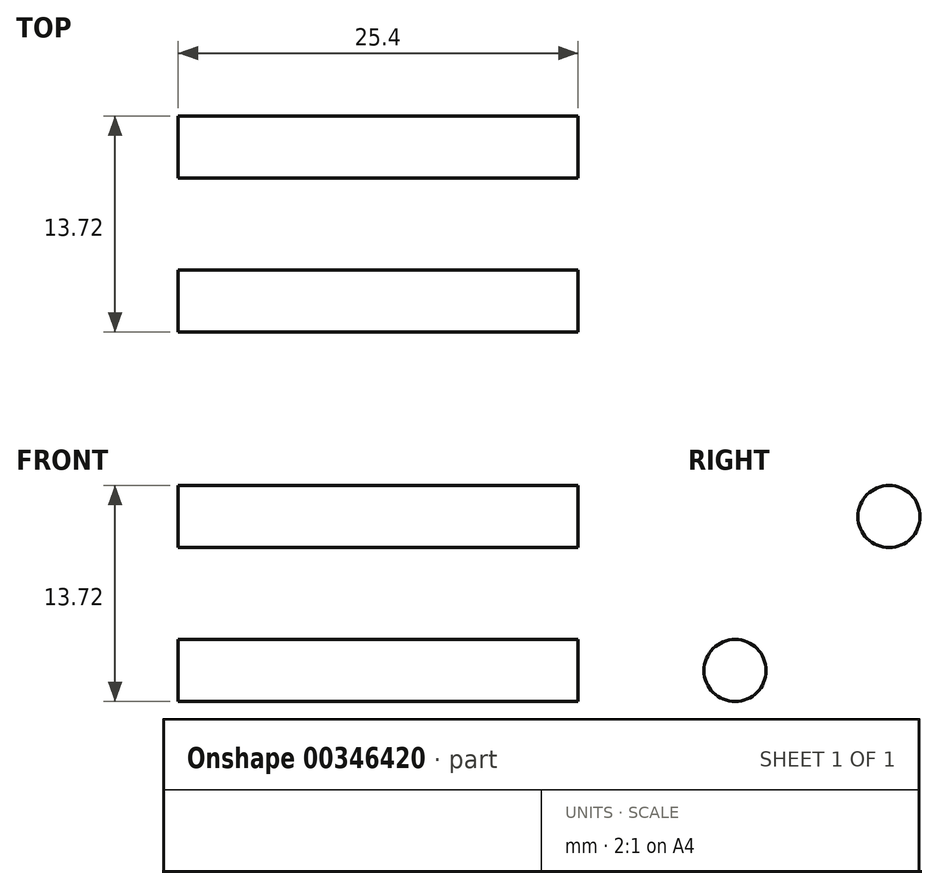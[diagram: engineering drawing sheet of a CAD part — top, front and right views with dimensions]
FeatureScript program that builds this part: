
annotation { "Feature Type Name" : "Feature", "Feature Type Description" : "" }
export const myFeature = defineFeature(function(context is Context, id is Id, definition is map)
    precondition{}
    {
        {
            var Q0;
            Q0=qCreatedBy(makeId("Front.planeOp"),FACE);
            var sketch = newSketch(context, id + "F0", { "sketchPlane" : qUnion([Q0])});
            skLineSegment(sketch, "E0.top", {"start": v(-34.36, 16.13) * mm, "end": v(-8.96, 16.13) * mm});
            skLineSegment(sketch, "E0.left", {"start": v(-34.36, 32) * mm, "end": v(-34.36, 16.13) * mm});
            skLineSegment(sketch, "E0.right", {"start": v(-8.96, 32) * mm, "end": v(-8.96, 16.13) * mm});
            skLineSegment(sketch, "E1", {"start": v(-34.36, 32) * mm, "end": v(-31.05, 32) * mm});
            skLineSegment(sketch, "E2", {"start": v(-12.26, 32) * mm, "end": v(-8.96, 32) * mm});
            skEllipticalArc(sketch, "E3", {});
            skPoint(sketch, "E4.visualSharp", {"position": v(-29.28, 32) * mm});
            skArc(sketch, "E4.filletArc", {"start": v(-28.9, 30.84) * mm, "mid": v(-29.83, 31.7) * mm, "end": v(-31.05, 32) * mm});
            skPoint(sketch, "E5.visualSharp", {"position": v(-14.04, 32) * mm});
            skArc(sketch, "E5.filletArc", {"start": v(-12.26, 32) * mm, "mid": v(-13.48, 31.7) * mm, "end": v(-14.4, 30.84) * mm});
            const initialGuessF0  = {"E3": [-0.02165555876195431, 0.03200357941810279, -1, 0, 0.00762, 0.00381, 0.3110816848913883, 2.8305109686984053]};
            skSetInitialGuess(sketch, initialGuessF0);
            skSolve(sketch);
        }
        {
            var Q0;
            Q0=makeQuery(id+"F0.imprint","IMPRINT",FACE,{"disambiguationData":[TD([[makeQuery(id+"F0.imprint","IMPRINT",EDGE,{"derivedFrom":sQuery(id+"F0.wireOp",EDGE,"E0.top")}),1.0]])]});
            var Q1;
            Q1=sQuery(id+"F0.wireOp",EDGE,"E0.top");
            revolve(context, id + "F1", {"entities" : qUnion([Q0]), "axis" : qUnion([Q1]), "revolveType" : RevolveType.FULL});
        }
        {
            var Q0;
            Q0=makeQuery(id+"F1.opRevolve","SWEPT_FACE",FACE,{"disambiguationData":[OSD([sQuery(id+"F0.wireOp",EDGE,"E0.right")])]});
            var sketch = newSketch(context, id + "F2", { "sketchPlane" : qUnion([Q0])});
            skCircle(sketch, "E6", {"center": v(0, 16.13) * mm, "radius": 9.78 * mm});
            skCircle(sketch, "E7", {"center": v(9.78, 16.13) * mm, "radius": 1.97 * mm});
            skCircle(sketch, "E8.1.0", {"center": v(6.91, 23.04) * mm, "radius": 1.97 * mm});
            skCircle(sketch, "E8.2.0", {"center": v(0, 25.9) * mm, "radius": 1.97 * mm});
            skCircle(sketch, "E8.3.0", {"center": v(-6.91, 23.04) * mm, "radius": 1.97 * mm});
            skCircle(sketch, "E8.4.0", {"center": v(-9.78, 16.13) * mm, "radius": 1.97 * mm});
            skCircle(sketch, "E8.5.0", {"center": v(-6.91, 9.21) * mm, "radius": 1.97 * mm});
            skCircle(sketch, "E8.6.0", {"center": v(0, 6.35) * mm, "radius": 1.97 * mm});
            skCircle(sketch, "E8.7.0", {"center": v(6.91, 9.21) * mm, "radius": 1.97 * mm});
            skCircle(sketch, "E9", {"center": v(0, 16.13) * mm, "radius": 3.56 * mm});
            skSolve(sketch);
        }
        {
            var Q0;
            {var subQ0=sQuery(id+"F2.wireOp",EDGE,"E8.1.0");var subQ1=sQuery(id+"F2.wireOp",EDGE,"E6");var subQ2=makeQuery(id+"F2.imprint","INTERSECT",VERTEX,{"disambiguationData":[OD(0.0)],"derivedFrom":[subQ1,subQ0]});Q0=makeQuery(id+"F2.imprint","IMPRINT",FACE,{"disambiguationData":[TD([[makeQuery(id+"F2.imprint","IMPRINT",EDGE,{"disambiguationData":[TD([[subQ2,-1.0]])],"derivedFrom":subQ1}),1.0]])]});}
            var Q1;
            {var subQ0=sQuery(id+"F2.wireOp",EDGE,"E8.1.0");var subQ1=sQuery(id+"F2.wireOp",EDGE,"E6");var subQ2=makeQuery(id+"F2.imprint","INTERSECT",VERTEX,{"disambiguationData":[OD(0.0)],"derivedFrom":[subQ1,subQ0]});Q1=makeQuery(id+"F2.imprint","IMPRINT",FACE,{"disambiguationData":[TD([[makeQuery(id+"F2.imprint","IMPRINT",EDGE,{"disambiguationData":[TD([[subQ2,-1.0]])],"derivedFrom":subQ1}),-1.0]])]});}
            var Q2;
            {var subQ0=sQuery(id+"F2.wireOp",EDGE,"E8.2.0");var subQ1=sQuery(id+"F2.wireOp",EDGE,"E6");var subQ2=makeQuery(id+"F2.imprint","INTERSECT",VERTEX,{"disambiguationData":[OD(0.0)],"derivedFrom":[subQ1,subQ0]});Q2=makeQuery(id+"F2.imprint","IMPRINT",FACE,{"disambiguationData":[TD([[makeQuery(id+"F2.imprint","IMPRINT",EDGE,{"disambiguationData":[TD([[subQ2,-1.0]])],"derivedFrom":subQ1}),1.0]])]});}
            var Q3;
            {var subQ0=sQuery(id+"F2.wireOp",EDGE,"E8.2.0");var subQ1=sQuery(id+"F2.wireOp",EDGE,"E6");var subQ2=makeQuery(id+"F2.imprint","INTERSECT",VERTEX,{"disambiguationData":[OD(0.0)],"derivedFrom":[subQ1,subQ0]});Q3=makeQuery(id+"F2.imprint","IMPRINT",FACE,{"disambiguationData":[TD([[makeQuery(id+"F2.imprint","IMPRINT",EDGE,{"disambiguationData":[TD([[subQ2,-1.0]])],"derivedFrom":subQ1}),-1.0]])]});}
            var Q4;
            {var subQ0=sQuery(id+"F2.wireOp",EDGE,"E8.3.0");var subQ1=sQuery(id+"F2.wireOp",EDGE,"E6");var subQ2=makeQuery(id+"F2.imprint","INTERSECT",VERTEX,{"disambiguationData":[OD(0.0)],"derivedFrom":[subQ1,subQ0]});Q4=makeQuery(id+"F2.imprint","IMPRINT",FACE,{"disambiguationData":[TD([[makeQuery(id+"F2.imprint","IMPRINT",EDGE,{"disambiguationData":[TD([[subQ2,-1.0]])],"derivedFrom":subQ1}),1.0]])]});}
            var Q5;
            {var subQ0=sQuery(id+"F2.wireOp",EDGE,"E8.3.0");var subQ1=sQuery(id+"F2.wireOp",EDGE,"E6");var subQ2=makeQuery(id+"F2.imprint","INTERSECT",VERTEX,{"disambiguationData":[OD(0.0)],"derivedFrom":[subQ1,subQ0]});Q5=makeQuery(id+"F2.imprint","IMPRINT",FACE,{"disambiguationData":[TD([[makeQuery(id+"F2.imprint","IMPRINT",EDGE,{"disambiguationData":[TD([[subQ2,-1.0]])],"derivedFrom":subQ1}),-1.0]])]});}
            var Q6;
            {var subQ0=sQuery(id+"F2.wireOp",EDGE,"E8.4.0");var subQ1=sQuery(id+"F2.wireOp",EDGE,"E6");var subQ2=makeQuery(id+"F2.imprint","INTERSECT",VERTEX,{"disambiguationData":[OD(0.0)],"derivedFrom":[subQ1,subQ0]});Q6=makeQuery(id+"F2.imprint","IMPRINT",FACE,{"disambiguationData":[TD([[makeQuery(id+"F2.imprint","IMPRINT",EDGE,{"disambiguationData":[TD([[subQ2,-1.0]])],"derivedFrom":subQ1}),1.0]])]});}
            var Q7;
            {var subQ0=sQuery(id+"F2.wireOp",EDGE,"E8.4.0");var subQ1=sQuery(id+"F2.wireOp",EDGE,"E6");var subQ2=makeQuery(id+"F2.imprint","INTERSECT",VERTEX,{"disambiguationData":[OD(0.0)],"derivedFrom":[subQ1,subQ0]});Q7=makeQuery(id+"F2.imprint","IMPRINT",FACE,{"disambiguationData":[TD([[makeQuery(id+"F2.imprint","IMPRINT",EDGE,{"disambiguationData":[TD([[subQ2,-1.0]])],"derivedFrom":subQ1}),-1.0]])]});}
            var Q8;
            {var subQ0=sQuery(id+"F2.wireOp",EDGE,"E8.5.0");var subQ1=sQuery(id+"F2.wireOp",EDGE,"E6");var subQ2=makeQuery(id+"F2.imprint","INTERSECT",VERTEX,{"disambiguationData":[OD(0.0)],"derivedFrom":[subQ1,subQ0]});Q8=makeQuery(id+"F2.imprint","IMPRINT",FACE,{"disambiguationData":[TD([[makeQuery(id+"F2.imprint","IMPRINT",EDGE,{"disambiguationData":[TD([[subQ2,-1.0]])],"derivedFrom":subQ1}),1.0]])]});}
            var Q9;
            {var subQ0=sQuery(id+"F2.wireOp",EDGE,"E8.5.0");var subQ1=sQuery(id+"F2.wireOp",EDGE,"E6");var subQ2=makeQuery(id+"F2.imprint","INTERSECT",VERTEX,{"disambiguationData":[OD(0.0)],"derivedFrom":[subQ1,subQ0]});Q9=makeQuery(id+"F2.imprint","IMPRINT",FACE,{"disambiguationData":[TD([[makeQuery(id+"F2.imprint","IMPRINT",EDGE,{"disambiguationData":[TD([[subQ2,-1.0]])],"derivedFrom":subQ1}),-1.0]])]});}
            var Q10;
            {var subQ0=sQuery(id+"F2.wireOp",EDGE,"E8.6.0");var subQ1=sQuery(id+"F2.wireOp",EDGE,"E6");var subQ2=makeQuery(id+"F2.imprint","INTERSECT",VERTEX,{"disambiguationData":[OD(0.0)],"derivedFrom":[subQ1,subQ0]});Q10=makeQuery(id+"F2.imprint","IMPRINT",FACE,{"disambiguationData":[TD([[makeQuery(id+"F2.imprint","IMPRINT",EDGE,{"disambiguationData":[TD([[subQ2,-1.0]])],"derivedFrom":subQ1}),1.0]])]});}
            var Q11;
            {var subQ0=sQuery(id+"F2.wireOp",EDGE,"E8.6.0");var subQ1=sQuery(id+"F2.wireOp",EDGE,"E6");var subQ2=makeQuery(id+"F2.imprint","INTERSECT",VERTEX,{"disambiguationData":[OD(0.0)],"derivedFrom":[subQ1,subQ0]});Q11=makeQuery(id+"F2.imprint","IMPRINT",FACE,{"disambiguationData":[TD([[makeQuery(id+"F2.imprint","IMPRINT",EDGE,{"disambiguationData":[TD([[subQ2,-1.0]])],"derivedFrom":subQ1}),-1.0]])]});}
            var Q12;
            {var subQ0=sQuery(id+"F2.wireOp",EDGE,"E8.7.0");var subQ1=sQuery(id+"F2.wireOp",EDGE,"E6");var subQ2=makeQuery(id+"F2.imprint","INTERSECT",VERTEX,{"disambiguationData":[OD(0.0)],"derivedFrom":[subQ1,subQ0]});Q12=makeQuery(id+"F2.imprint","IMPRINT",FACE,{"disambiguationData":[TD([[makeQuery(id+"F2.imprint","IMPRINT",EDGE,{"disambiguationData":[TD([[subQ2,-1.0]])],"derivedFrom":subQ1}),1.0]])]});}
            var Q13;
            {var subQ0=sQuery(id+"F2.wireOp",EDGE,"E8.7.0");var subQ1=sQuery(id+"F2.wireOp",EDGE,"E6");var subQ2=makeQuery(id+"F2.imprint","INTERSECT",VERTEX,{"disambiguationData":[OD(0.0)],"derivedFrom":[subQ1,subQ0]});Q13=makeQuery(id+"F2.imprint","IMPRINT",FACE,{"disambiguationData":[TD([[makeQuery(id+"F2.imprint","IMPRINT",EDGE,{"disambiguationData":[TD([[subQ2,-1.0]])],"derivedFrom":subQ1}),-1.0]])]});}
            var Q14;
            {var subQ0=sQuery(id+"F2.wireOp",EDGE,"E7");var subQ1=sQuery(id+"F2.wireOp",EDGE,"E6");var subQ2=makeQuery(id+"F2.imprint","INTERSECT",VERTEX,{"disambiguationData":[OD(0.0)],"derivedFrom":[subQ1,subQ0]});Q14=makeQuery(id+"F2.imprint","IMPRINT",FACE,{"disambiguationData":[TD([[makeQuery(id+"F2.imprint","IMPRINT",EDGE,{"disambiguationData":[TD([[subQ2,1.0]])],"derivedFrom":subQ1}),1.0]])]});}
            var Q15;
            {var subQ0=sQuery(id+"F2.wireOp",EDGE,"E7");var subQ1=sQuery(id+"F2.wireOp",EDGE,"E6");var subQ2=makeQuery(id+"F2.imprint","INTERSECT",VERTEX,{"disambiguationData":[OD(0.0)],"derivedFrom":[subQ1,subQ0]});Q15=makeQuery(id+"F2.imprint","IMPRINT",FACE,{"disambiguationData":[TD([[makeQuery(id+"F2.imprint","IMPRINT",EDGE,{"disambiguationData":[TD([[subQ2,1.0]])],"derivedFrom":subQ1}),-1.0]])]});}
            var Q16;
            Q16=makeQuery(id+"F2.imprint","IMPRINT",FACE,{"disambiguationData":[TD([[makeQuery(id+"F2.imprint","IMPRINT",EDGE,{"derivedFrom":sQuery(id+"F2.wireOp",EDGE,"E9")}),1.0]])]});
            extrude(context, id + "F3", {"entities" : qUnion([Q0, Q1, Q2, Q3, Q4, Q5, Q6, Q7, Q8, Q9, Q10, Q11, Q12, Q13, Q14, Q15, Q16]), "operationType" : NewBodyOperationType.REMOVE, "oppositeDirection" : true, "depth" : 25.4 * mm});
        }
    });
